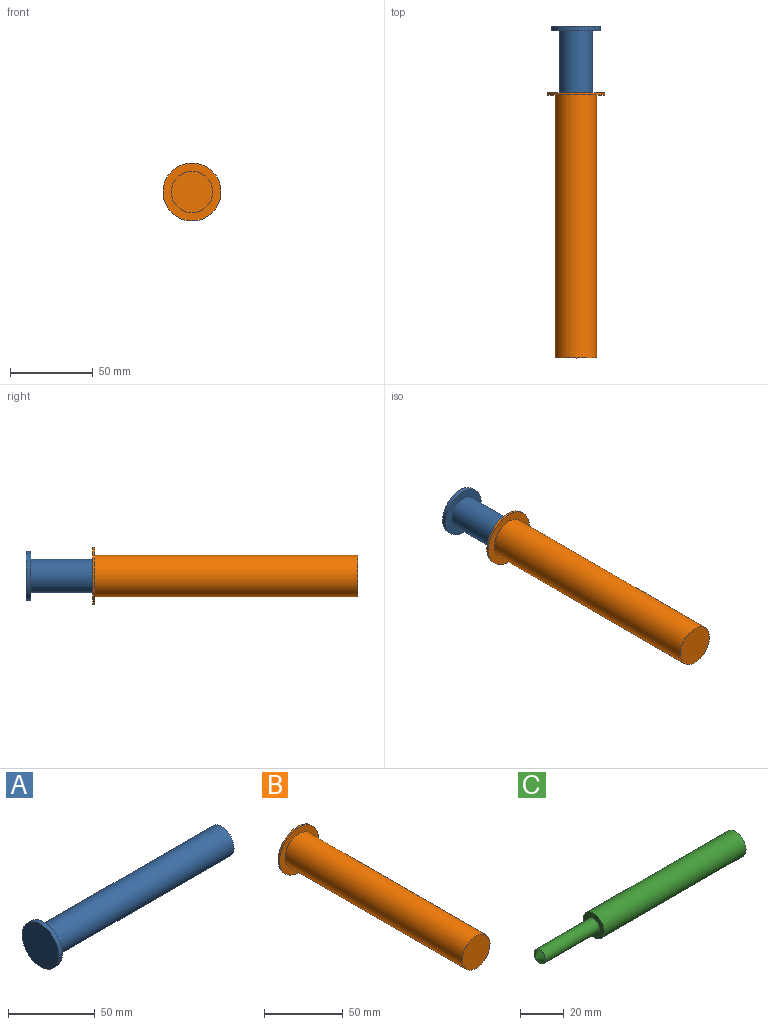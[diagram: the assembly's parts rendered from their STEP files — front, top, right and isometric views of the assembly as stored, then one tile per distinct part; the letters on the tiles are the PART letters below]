
ASSEMBLY  parts=3 mates=3
PART A: 7 faces, bbox 147.8x30.1x30.1 mm
  f0: plane 20x20mm, normal (1,0,0), area 125.5mm2, adj f1,f6
  f1: cylinder r=10mm len=145mm, axis (-1,0,0), area 9110.6mm2, adj f0,f2
  f2: plane 30.08x30.08mm, normal (1,0,0), area 396.4mm2, adj f1,f3
  f3: cylinder r=15.04mm len=30.08mm, axis (-1,0,0), area 265.5mm2, adj f2,f4
  f4: plane 30.08x30.08mm, normal (-1,0,0), area 710.6mm2, adj f3
  f5: cone r=0mm half-angle=59deg, axis (1,0,0), area 220.1mm2, adj f6
  f6: cylinder r=7.75mm len=85mm, axis (1,0,0), area 4139mm2, adj f0,f5
PART B: 7 faces, bbox 35x160x35 mm
  f0: cylinder r=12.5mm len=158.7mm, axis (0,1,0), area 12464.3mm2, adj f1,f3
  f1: plane 25x25mm, normal (0,-1,0), area 490.9mm2, adj f0
  f2: cylinder r=17.5mm len=35mm, axis (0,1,0), area 142.9mm2, adj f3,f4
  f3: plane 35x35mm, normal (0,-1,0), area 471.2mm2, adj f0,f2
  f4: plane 35x35mm, normal (0,1,0), area 648mm2, adj f2,f5
  f5: cylinder r=10mm len=157.5mm, axis (0,1,0), area 9896mm2, adj f4,f6
  f6: plane 20x20mm, normal (0,1,0), area 314.2mm2, adj f5
PART C: 5 faces, bbox 129.9x13.5x13.5 mm
  f0: plane 13.5x13.5mm, normal (1,0,0), area 143.1mm2, adj f1
  f1: cylinder r=6.75mm len=92mm, axis (-1,0,0), area 3901.9mm2, adj f0,f2
  f2: plane 13.5x13.5mm, normal (-1,0,0), area 99mm2, adj f1,f3
  f3: cylinder r=3.75mm len=35mm, axis (-1,0,0), area 824.7mm2, adj f2,f4
  f4: cone r=3.75mm half-angle=52.1deg, axis (1,0,0), area 56mm2, adj f3
PLACE A rot(axis=(0.58,-0.58,-0.58),120deg) t=(0,22.22,0)mm
PLACE B at identity fixed
PLACE C rot(axis=(0.58,-0.58,-0.58),120deg) t=(0,-78.01,0)mm
MATE slider A.f5 <-> B.f0  axis (0,1,0) through (0,-35,0)mm
MATE planar B.f0 <-> C.f4  axis (0,1,0) through (0,-160,0)mm
MATE slider C.f4 <-> B.f0  axis (0,1,0) through (0,-111.5,0)mm
